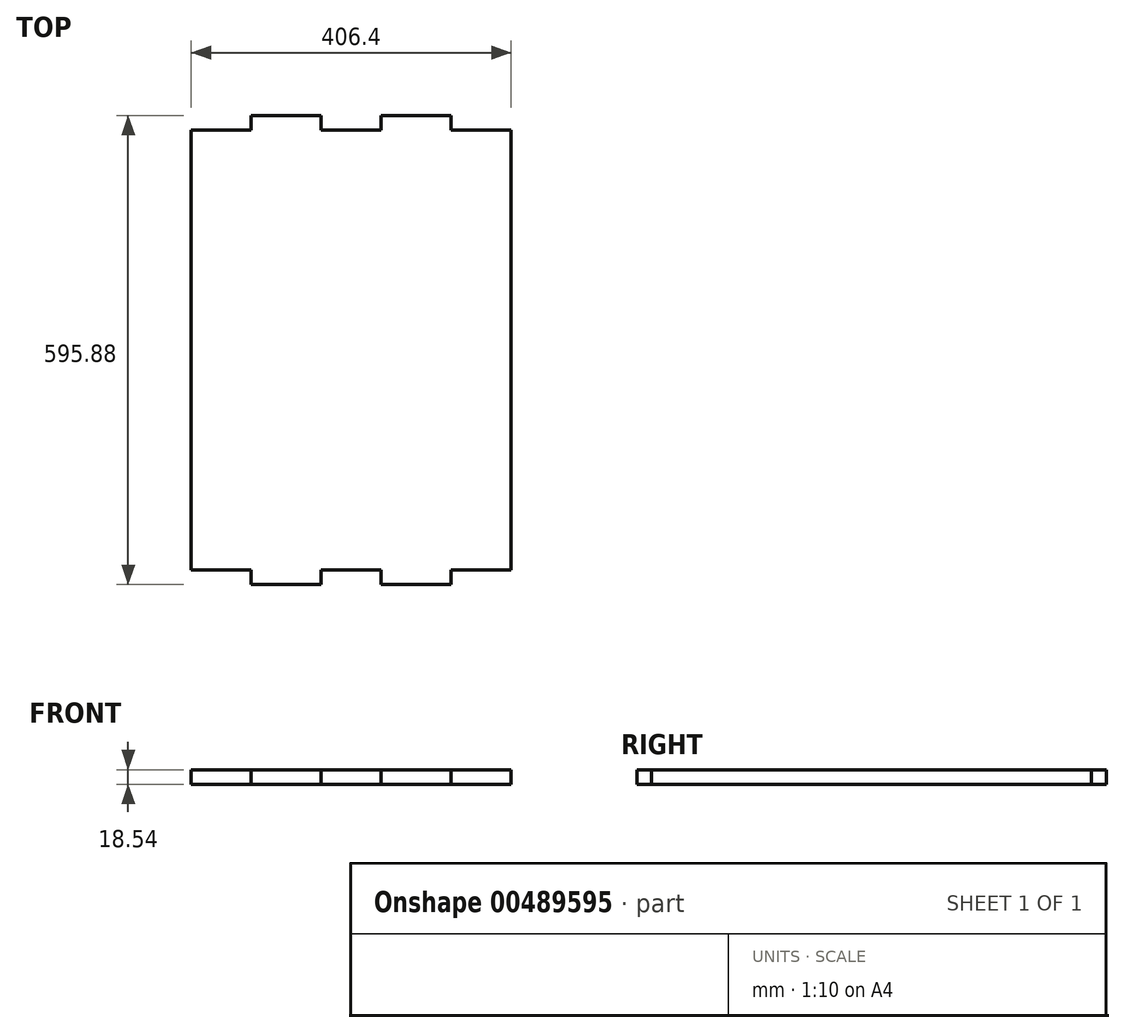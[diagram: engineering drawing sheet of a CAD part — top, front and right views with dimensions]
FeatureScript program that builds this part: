
annotation { "Feature Type Name" : "Feature", "Feature Type Description" : "" }
export const myFeature = defineFeature(function(context is Context, id is Id, definition is map)
    precondition{}
    {
        {
            var Q0;
            Q0=qCreatedBy(makeId("Top.planeOp"),FACE);
            var sketch = newSketch(context, id + "F0", { "sketchPlane" : qUnion([Q0])});
            skLineSegment(sketch, "E0.bottom", {"start": v(-203.42, 410.66) * mm, "end": v(202.98, 410.66) * mm});
            skLineSegment(sketch, "E0.top", {"start": v(-203.42, -148.14) * mm, "end": v(202.98, -148.14) * mm});
            skLineSegment(sketch, "E0.left", {"start": v(-203.42, 410.66) * mm, "end": v(-203.42, -148.14) * mm});
            skLineSegment(sketch, "E0.right", {"start": v(202.98, 410.66) * mm, "end": v(202.98, -148.14) * mm});
            skSolve(sketch);
        }
        {
            var Q0;
            Q0 = qSketchRegion(id + "F0", true);
            extrude(context, id + "F1", {"entities" : qUnion([Q0]), "depth" : 18.54 * mm, "offsetDistance" : 25.4 * mm});
        }
        {
            var Q0;
            Q0=makeQuery(id+"F1.opExtrude","SWEPT_FACE",FACE,{"disambiguationData":[OSD([sQuery(id+"F0.wireOp",EDGE,"E0.top")])]});
            var sketch = newSketch(context, id + "F2", { "sketchPlane" : qUnion([Q0])});
            skLineSegment(sketch, "E1", {"start": v(-203.42, 18.54) * mm, "end": v(-127.22, 18.54) * mm});
            skLineSegment(sketch, "E2", {"start": v(202.98, 18.54) * mm, "end": v(126.78, 18.54) * mm});
            skLineSegment(sketch, "E3", {"start": v(-127.22, 18.54) * mm, "end": v(-38.32, 18.54) * mm});
            skLineSegment(sketch, "E4", {"start": v(126.78, 18.54) * mm, "end": v(37.88, 18.54) * mm});
            skLineSegment(sketch, "E5", {"start": v(-127.22, 18.54) * mm, "end": v(-127.22, 0) * mm});
            skLineSegment(sketch, "E6", {"start": v(-38.32, 18.54) * mm, "end": v(-38.32, 0) * mm});
            skLineSegment(sketch, "E7", {"start": v(-38.32, 0) * mm, "end": v(-127.22, 0) * mm});
            skLineSegment(sketch, "E8", {"start": v(37.88, 18.54) * mm, "end": v(37.88, 0) * mm});
            skLineSegment(sketch, "E9", {"start": v(126.78, 18.54) * mm, "end": v(126.78, 0) * mm});
            skLineSegment(sketch, "E10", {"start": v(126.78, 0) * mm, "end": v(37.88, 0) * mm});
            skSolve(sketch);
        }
        {
            var Q0;
            Q0 = qSketchRegion(id + "F2", true);
            extrude(context, id + "F3", {"entities" : qUnion([Q0]), "operationType" : NewBodyOperationType.ADD, "depth" : 18.54 * mm, "offsetDistance" : 25.4 * mm});
        }
        {
            var Q0;
            Q0=makeQuery(id+"F1.opExtrude","SWEPT_FACE",FACE,{"disambiguationData":[OSD([sQuery(id+"F0.wireOp",EDGE,"E0.bottom")])]});
            var sketch = newSketch(context, id + "F4", { "sketchPlane" : qUnion([Q0])});
            skLineSegment(sketch, "E11", {"start": v(-202.98, 18.54) * mm, "end": v(-126.78, 18.54) * mm});
            skLineSegment(sketch, "E12", {"start": v(-126.78, 18.54) * mm, "end": v(-37.88, 18.54) * mm});
            skLineSegment(sketch, "E13", {"start": v(203.42, 18.54) * mm, "end": v(127.22, 18.54) * mm});
            skLineSegment(sketch, "E14", {"start": v(127.22, 18.54) * mm, "end": v(38.32, 18.54) * mm});
            skLineSegment(sketch, "E15", {"start": v(-126.78, 18.54) * mm, "end": v(-126.78, 0) * mm});
            skLineSegment(sketch, "E16", {"start": v(-126.78, 0) * mm, "end": v(-37.88, 0) * mm});
            skLineSegment(sketch, "E17", {"start": v(-37.88, 0) * mm, "end": v(-37.88, 18.54) * mm});
            skLineSegment(sketch, "E18", {"start": v(38.32, 18.54) * mm, "end": v(38.32, 0) * mm});
            skLineSegment(sketch, "E19", {"start": v(38.32, 0) * mm, "end": v(127.22, 0) * mm});
            skLineSegment(sketch, "E20", {"start": v(127.22, 18.54) * mm, "end": v(127.22, 0) * mm});
            skSolve(sketch);
        }
        {
            var Q0;
            Q0 = qSketchRegion(id + "F4", true);
            extrude(context, id + "F5", {"entities" : qUnion([Q0]), "operationType" : NewBodyOperationType.ADD, "depth" : 18.54 * mm, "offsetDistance" : 25.4 * mm});
        }
    });
